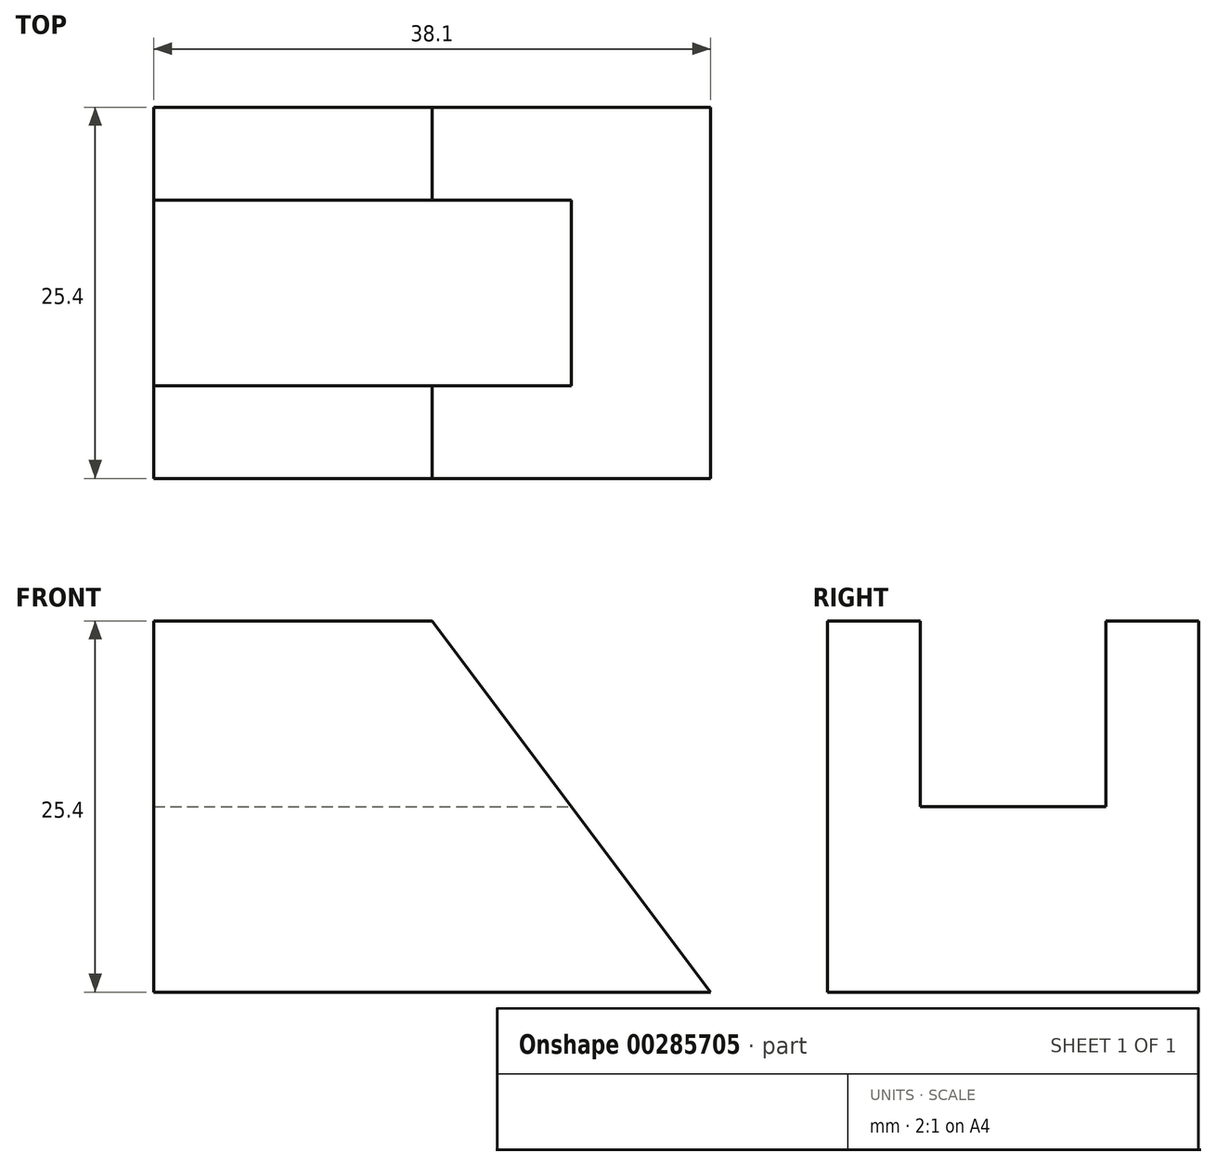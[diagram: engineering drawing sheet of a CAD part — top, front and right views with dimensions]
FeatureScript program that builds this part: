
annotation { "Feature Type Name" : "Feature", "Feature Type Description" : "" }
export const myFeature = defineFeature(function(context is Context, id is Id, definition is map)
    precondition{}
    {
        {
            var Q0;
            Q0=qCreatedBy(makeId("Front.planeOp"),FACE);
            var sketch = newSketch(context, id + "F0", { "sketchPlane" : qUnion([Q0])});
            skLineSegment(sketch, "E0.bottom", {"start": v(0, 0) * mm, "end": v(38.1, 0) * mm});
            skLineSegment(sketch, "E0.top", {"start": v(0, 25.4) * mm, "end": v(38.1, 25.4) * mm});
            skLineSegment(sketch, "E0.left", {"start": v(0, 0) * mm, "end": v(0, 25.4) * mm});
            skLineSegment(sketch, "E0.right", {"start": v(38.1, 0) * mm, "end": v(38.1, 25.4) * mm});
            skLineSegment(sketch, "E1", {"start": v(19.05, 25.4) * mm, "end": v(38.1, 0) * mm});
            skLineSegment(sketch, "E2", {"start": v(38.1, 25.4) * mm, "end": v(19.05, 25.4) * mm});
            skSolve(sketch);
        }
        {
            var Q0;
            Q0=makeQuery(id+"F0.imprint","IMPRINT",FACE,{"disambiguationData":[TD([[makeQuery(id+"F0.imprint","IMPRINT",EDGE,{"derivedFrom":sQuery(id+"F0.wireOp",EDGE,"E0.bottom")}),1.0]])]});
            extrude(context, id + "F1", {"entities" : qUnion([Q0]), "endBound" : BoundingType.SYMMETRIC, "oppositeDirection" : true, "depth" : 25.4 * mm});
        }
        {
            var Q0;
            Q0=qCreatedBy(makeId("Front.planeOp"),FACE);
            var sketch = newSketch(context, id + "F2", { "sketchPlane" : qUnion([Q0])});
            skLineSegment(sketch, "E3", {"start": v(0, 25.4) * mm, "end": v(19.05, 25.4) * mm});
            skLineSegment(sketch, "E4", {"start": v(0, 25.4) * mm, "end": v(0, 12.7) * mm});
            skLineSegment(sketch, "E5", {"start": v(0, 12.7) * mm, "end": v(28.57, 12.7) * mm});
            skLineSegment(sketch, "E6", {"start": v(28.58, 12.7) * mm, "end": v(19.05, 25.4) * mm});
            skSolve(sketch);
        }
        {
            var Q0;
            Q0 = qSketchRegion(id + "F2", true);
            extrude(context, id + "F3", {"entities" : qUnion([Q0]), "operationType" : NewBodyOperationType.REMOVE, "endBound" : BoundingType.SYMMETRIC, "oppositeDirection" : true, "depth" : 12.7 * mm});
        }
    });
